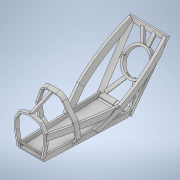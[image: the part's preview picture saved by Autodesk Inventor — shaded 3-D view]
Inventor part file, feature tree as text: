
AUTODESK INVENTOR PART (.ipt)
format: ipt  version: 2020 (Build 240168000, 168)  size: 480,256 bytes
history: native  units: in
note: dims shown in document units (in); Inventor stores cm internally (conversion verified against a paired STEP export)
features: sketch x2, other x1, extrude x1, pattern_circular x1
ambient origin geometry x8: Origin, YZ Plane, XZ Plane, XY Plane, X Axis, Y Axis, Z Axis, Center Point
bodies: Solid1 (feature_tree), Solid4 (feature_tree)
feature tree (5):
  other  "Repaired Geometry1"
  extrude  "Extrusion1"  Depth=1.1811in TaperAngle=0.0deg
  pattern_circular  "Circular Pattern1"  Count=4  [1 undecoded]
  sketch  "3D Sketch1"
  sketch  "Sketch1"  dims[d0=0.7874in d1=1.1811in d2=0.0in d3=1.5748in d4=2.4737in]
note: 1 required parameter value undecoded (feature->parameter linkage not recoverable at this tier; creation-order binding heuristic only, values carry confidence <= 0.55)
